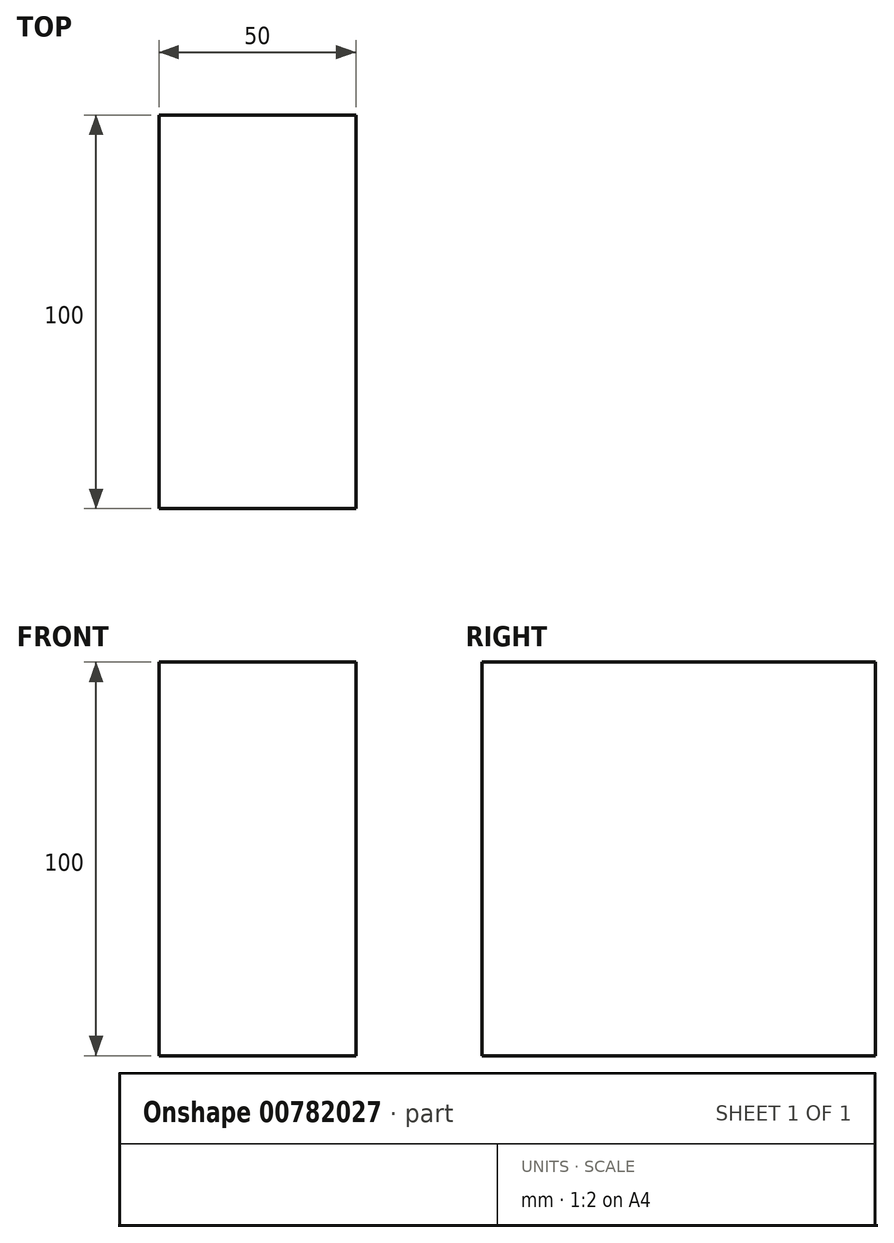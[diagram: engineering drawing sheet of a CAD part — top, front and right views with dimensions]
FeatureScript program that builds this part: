
annotation { "Feature Type Name" : "Feature", "Feature Type Description" : "" }
export const myFeature = defineFeature(function(context is Context, id is Id, definition is map)
    precondition{}
    {
        {
            var Q0;
            Q0=qCreatedBy(makeId("Top.planeOp"),FACE);
            var sketch = newSketch(context, id + "F0", { "sketchPlane" : qUnion([Q0])});
            skLineSegment(sketch, "E0.bottom", {"start": v(25, 50) * mm, "end": v(-25, 50) * mm});
            skLineSegment(sketch, "E0.top", {"start": v(25, -50) * mm, "end": v(-25, -50) * mm});
            skLineSegment(sketch, "E0.left", {"start": v(25, 50) * mm, "end": v(25, -50) * mm});
            skLineSegment(sketch, "E0.right", {"start": v(-25, 50) * mm, "end": v(-25, -50) * mm});
            skPoint(sketch, "E0.middle", {"position": v(0, 0) * mm});
            skSolve(sketch);
        }
        {
            var Q0;
            Q0=makeQuery(id+"F0.imprint","IMPRINT",FACE,{"disambiguationData":[TD([[makeQuery(id+"F0.imprint","IMPRINT",EDGE,{"derivedFrom":sQuery(id+"F0.wireOp",EDGE,"E0.bottom")}),1.0]])]});
            extrude(context, id + "F1", {"entities" : qUnion([Q0]), "depth" : 100 * mm, "offsetDistance" : 25 * mm});
        }
    });
